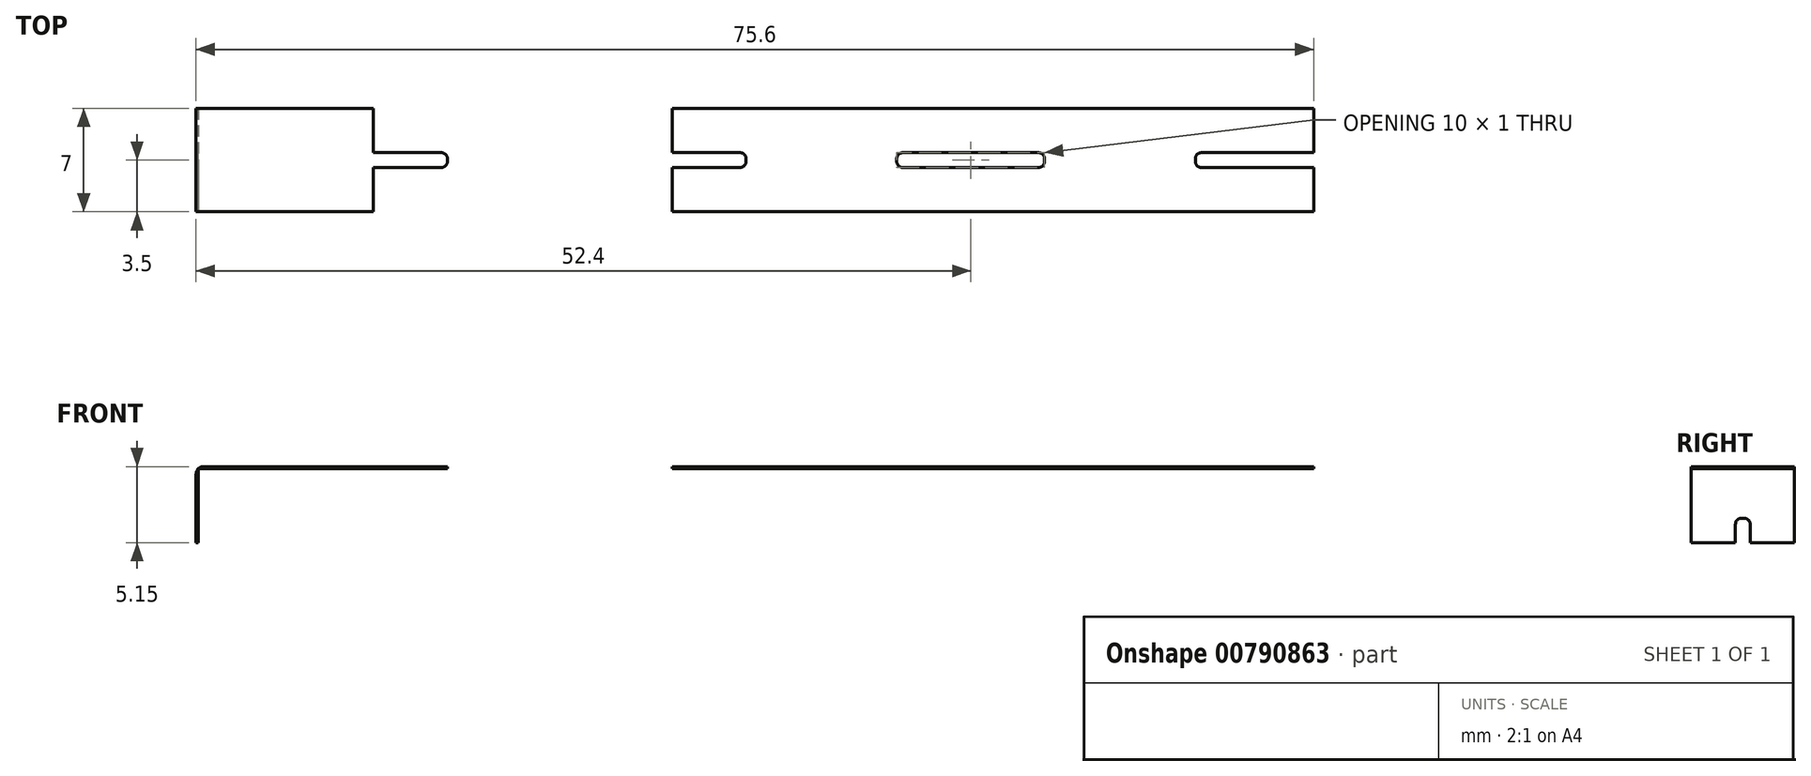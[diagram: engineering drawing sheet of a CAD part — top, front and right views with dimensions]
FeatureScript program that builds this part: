
annotation { "Feature Type Name" : "Feature", "Feature Type Description" : "" }
export const myFeature = defineFeature(function(context is Context, id is Id, definition is map)
    precondition{}
    {
        {
            var Q0;
            Q0=qCreatedBy(makeId("Top.planeOp"),FACE);
            var sketch = newSketch(context, id + "F0", { "sketchPlane" : qUnion([Q0])});
            skPoint(sketch, "E0.middle", {"position": v(0, 0) * mm});
            skLineSegment(sketch, "E1.bottom", {"start": v(-5.5, -0.5) * mm, "end": v(-10.1, -0.5) * mm});
            skLineSegment(sketch, "E1.top", {"start": v(-5.5, 0.5) * mm, "end": v(-10.1, 0.5) * mm});
            skLineSegment(sketch, "E1.left", {"start": v(-5.1, -0.1) * mm, "end": v(-5.1, 0.1) * mm});
            skLineSegment(sketch, "E1.right", {"start": v(-15.1, -0.1) * mm, "end": v(-15.1, 0.1) * mm});
            skPoint(sketch, "E1.middle", {"position": v(-10.1, 0) * mm});
            skPoint(sketch, "E2.visualSharp", {"position": v(-5.1, 0.5) * mm});
            skArc(sketch, "E2.filletArc", {"start": v(-5.1, 0.1) * mm, "mid": v(-5.22, 0.38) * mm, "end": v(-5.5, 0.5) * mm});
            skPoint(sketch, "E3.visualSharp", {"position": v(-5.1, -0.5) * mm});
            skArc(sketch, "E3.filletArc", {"start": v(-5.5, -0.5) * mm, "mid": v(-5.22, -0.38) * mm, "end": v(-5.1, -0.1) * mm});
            skPoint(sketch, "E4.visualSharp", {"position": v(-15.1, 0.5) * mm});
            skArc(sketch, "E4.filletArc", {"start": v(-14.7, 0.5) * mm, "mid": v(-14.98, 0.38) * mm, "end": v(-15.1, 0.1) * mm});
            skPoint(sketch, "E5.visualSharp", {"position": v(-15.1, -0.5) * mm});
            skArc(sketch, "E5.filletArc", {"start": v(-15.1, -0.1) * mm, "mid": v(-14.98, -0.38) * mm, "end": v(-14.7, -0.5) * mm});
            skLineSegment(sketch, "E6", {"start": v(0, 3.5) * mm, "end": v(-10.1, 3.5) * mm});
            skPoint(sketch, "E6.endSnap0", {"position": v(-10.1, 0.5) * mm});
            skLineSegment(sketch, "E7", {"start": v(-10.1, 3.5) * mm, "end": v(-10.1, 0.5) * mm});
            skLineSegment(sketch, "E8.MirrorCS", {"start": v(0, -3.5) * mm, "end": v(-10.1, -3.5) * mm});
            skLineSegment(sketch, "E9.MirrorCS", {"start": v(-10.1, -3.5) * mm, "end": v(-10.1, -0.5) * mm});
            skLineSegment(sketch, "E10.MirrorCS", {"start": v(0, 3.5) * mm, "end": v(10.1, 3.5) * mm});
            skLineSegment(sketch, "E11.MirrorCS", {"start": v(0, -3.5) * mm, "end": v(10.1, -3.5) * mm});
            skLineSegment(sketch, "E12.MirrorCS", {"start": v(5.1, -0.1) * mm, "end": v(5.1, 0.1) * mm});
            skArc(sketch, "E13.MirrorCS", {"start": v(5.1, 0.1) * mm, "mid": v(5.22, 0.38) * mm, "end": v(5.5, 0.5) * mm});
            skArc(sketch, "E14.MirrorCS", {"start": v(15.1, -0.1) * mm, "mid": v(14.98, -0.38) * mm, "end": v(14.7, -0.5) * mm});
            skLineSegment(sketch, "E15.MirrorCS", {"start": v(15.1, -0.1) * mm, "end": v(15.1, 0.1) * mm});
            skArc(sketch, "E16.MirrorCS", {"start": v(14.7, 0.5) * mm, "mid": v(14.98, 0.38) * mm, "end": v(15.1, 0.1) * mm});
            skArc(sketch, "E17.MirrorCS", {"start": v(5.5, -0.5) * mm, "mid": v(5.22, -0.38) * mm, "end": v(5.1, -0.1) * mm});
            skPoint(sketch, "E18.MirrorP", {"position": v(15.1, 0.5) * mm});
            skLineSegment(sketch, "E19.MirrorCS", {"start": v(5.5, 0.5) * mm, "end": v(14.7, 0.5) * mm});
            skLineSegment(sketch, "E20.MirrorCS", {"start": v(5.5, -0.5) * mm, "end": v(14.7, -0.5) * mm});
            skPoint(sketch, "E21.MirrorP", {"position": v(10.1, 0.5) * mm});
            skPoint(sketch, "E22.MirrorP", {"position": v(5.1, 0.5) * mm});
            skPoint(sketch, "E23.MirrorP", {"position": v(15.1, -0.5) * mm});
            skPoint(sketch, "E24.MirrorP", {"position": v(5.1, -0.5) * mm});
            skPoint(sketch, "E25.MirrorP", {"position": v(10.1, 0) * mm});
            skLineSegment(sketch, "E26.MirrorCS", {"start": v(10.1, 3.5) * mm, "end": v(10.1, 0.5) * mm});
            skLineSegment(sketch, "E27.MirrorCS", {"start": v(10.1, -3.5) * mm, "end": v(10.1, -0.5) * mm});
            skPoint(sketch, "E28.1.0.0", {"position": v(25.3, 0.5) * mm});
            skLineSegment(sketch, "E28.1.0.1", {"start": v(20.2, 3.5) * mm, "end": v(30.3, 3.5) * mm});
            skLineSegment(sketch, "E28.1.0.2", {"start": v(25.7, -0.5) * mm, "end": v(34.9, -0.5) * mm});
            skPoint(sketch, "E28.1.0.3", {"position": v(20.2, 0) * mm});
            skLineSegment(sketch, "E28.1.0.4", {"start": v(20.2, -3.5) * mm, "end": v(30.3, -3.5) * mm});
            skPoint(sketch, "E28.1.0.5", {"position": v(30.3, 0.5) * mm});
            skPoint(sketch, "E28.1.0.6", {"position": v(30.3, 0) * mm});
            skPoint(sketch, "E28.1.0.7", {"position": v(35.3, -0.5) * mm});
            skPoint(sketch, "E28.1.0.8", {"position": v(25.3, -0.5) * mm});
            skLineSegment(sketch, "E28.1.0.9", {"start": v(20.2, -3.5) * mm, "end": v(10.1, -3.5) * mm});
            skLineSegment(sketch, "E28.1.0.10", {"start": v(25.7, 0.5) * mm, "end": v(34.9, 0.5) * mm});
            skLineSegment(sketch, "E28.1.0.11", {"start": v(20.2, 3.5) * mm, "end": v(10.1, 3.5) * mm});
            skLineSegment(sketch, "E28.1.0.12", {"start": v(30.3, 3.5) * mm, "end": v(30.3, 0.5) * mm});
            skLineSegment(sketch, "E28.1.0.13", {"start": v(30.3, -3.5) * mm, "end": v(30.3, -0.5) * mm});
            skPoint(sketch, "E28.1.0.14", {"position": v(35.3, 0.5) * mm});
            skArc(sketch, "E28.1.0.15", {"start": v(34.9, 0.5) * mm, "mid": v(35.18, 0.38) * mm, "end": v(35.3, 0.1) * mm});
            skArc(sketch, "E28.1.0.16", {"start": v(25.7, -0.5) * mm, "mid": v(25.42, -0.38) * mm, "end": v(25.3, -0.1) * mm});
            skArc(sketch, "E28.1.0.17", {"start": v(35.3, -0.1) * mm, "mid": v(35.18, -0.38) * mm, "end": v(34.9, -0.5) * mm});
            skArc(sketch, "E28.1.0.18", {"start": v(25.3, 0.1) * mm, "mid": v(25.42, 0.38) * mm, "end": v(25.7, 0.5) * mm});
            skLineSegment(sketch, "E28.1.0.19", {"start": v(25.3, -0.1) * mm, "end": v(25.3, 0.1) * mm});
            skLineSegment(sketch, "E28.1.0.20", {"start": v(35.3, -0.1) * mm, "end": v(35.3, 0.1) * mm});
            skPoint(sketch, "E28.2.0.0", {"position": v(45.5, 0.5) * mm});
            skLineSegment(sketch, "E28.2.0.1", {"start": v(40.4, 3.5) * mm, "end": v(50.5, 3.5) * mm});
            skLineSegment(sketch, "E28.2.0.2", {"start": v(45.9, -0.5) * mm, "end": v(55.1, -0.5) * mm});
            skPoint(sketch, "E28.2.0.3", {"position": v(40.4, 0) * mm});
            skLineSegment(sketch, "E28.2.0.4", {"start": v(40.4, -3.5) * mm, "end": v(50.5, -3.5) * mm});
            skPoint(sketch, "E28.2.0.5", {"position": v(50.5, 0.5) * mm});
            skPoint(sketch, "E28.2.0.6", {"position": v(50.5, 0) * mm});
            skPoint(sketch, "E28.2.0.7", {"position": v(55.5, -0.5) * mm});
            skPoint(sketch, "E28.2.0.8", {"position": v(45.5, -0.5) * mm});
            skLineSegment(sketch, "E28.2.0.9", {"start": v(40.4, -3.5) * mm, "end": v(30.3, -3.5) * mm});
            skLineSegment(sketch, "E28.2.0.10", {"start": v(45.9, 0.5) * mm, "end": v(55.1, 0.5) * mm});
            skLineSegment(sketch, "E28.2.0.11", {"start": v(40.4, 3.5) * mm, "end": v(30.3, 3.5) * mm});
            skLineSegment(sketch, "E28.2.0.12", {"start": v(50.5, 3.5) * mm, "end": v(50.5, 0.5) * mm});
            skLineSegment(sketch, "E28.2.0.13", {"start": v(50.5, -3.5) * mm, "end": v(50.5, -0.5) * mm});
            skPoint(sketch, "E28.2.0.14", {"position": v(55.5, 0.5) * mm});
            skArc(sketch, "E28.2.0.15", {"start": v(55.1, 0.5) * mm, "mid": v(55.38, 0.38) * mm, "end": v(55.5, 0.1) * mm});
            skArc(sketch, "E28.2.0.16", {"start": v(45.9, -0.5) * mm, "mid": v(45.62, -0.38) * mm, "end": v(45.5, -0.1) * mm});
            skArc(sketch, "E28.2.0.17", {"start": v(55.5, -0.1) * mm, "mid": v(55.38, -0.38) * mm, "end": v(55.1, -0.5) * mm});
            skArc(sketch, "E28.2.0.18", {"start": v(45.5, 0.1) * mm, "mid": v(45.62, 0.38) * mm, "end": v(45.9, 0.5) * mm});
            skLineSegment(sketch, "E28.2.0.19", {"start": v(45.5, -0.1) * mm, "end": v(45.5, 0.1) * mm});
            skLineSegment(sketch, "E28.2.0.20", {"start": v(55.5, -0.1) * mm, "end": v(55.5, 0.1) * mm});
            skPoint(sketch, "E28.3.0.0", {"position": v(65.7, 0.5) * mm});
            skLineSegment(sketch, "E28.3.0.1", {"start": v(60.6, 3.5) * mm, "end": v(70.7, 3.5) * mm});
            skLineSegment(sketch, "E28.3.0.2", {"start": v(66.1, -0.5) * mm, "end": v(75.3, -0.5) * mm});
            skPoint(sketch, "E28.3.0.3", {"position": v(60.6, 0) * mm});
            skLineSegment(sketch, "E28.3.0.4", {"start": v(60.6, -3.5) * mm, "end": v(70.7, -3.5) * mm});
            skPoint(sketch, "E28.3.0.5", {"position": v(70.7, 0.5) * mm});
            skPoint(sketch, "E28.3.0.6", {"position": v(70.7, 0) * mm});
            skPoint(sketch, "E28.3.0.7", {"position": v(75.7, -0.5) * mm});
            skPoint(sketch, "E28.3.0.8", {"position": v(65.7, -0.5) * mm});
            skLineSegment(sketch, "E28.3.0.9", {"start": v(60.6, -3.5) * mm, "end": v(50.5, -3.5) * mm});
            skLineSegment(sketch, "E28.3.0.10", {"start": v(66.1, 0.5) * mm, "end": v(75.3, 0.5) * mm});
            skLineSegment(sketch, "E28.3.0.11", {"start": v(60.6, 3.5) * mm, "end": v(50.5, 3.5) * mm});
            skLineSegment(sketch, "E28.3.0.12", {"start": v(70.7, 3.5) * mm, "end": v(70.7, 0.5) * mm});
            skLineSegment(sketch, "E28.3.0.13", {"start": v(70.7, -3.5) * mm, "end": v(70.7, -0.5) * mm});
            skPoint(sketch, "E28.3.0.14", {"position": v(75.7, 0.5) * mm});
            skArc(sketch, "E28.3.0.15", {"start": v(75.3, 0.5) * mm, "mid": v(75.58, 0.38) * mm, "end": v(75.7, 0.1) * mm});
            skArc(sketch, "E28.3.0.16", {"start": v(66.1, -0.5) * mm, "mid": v(65.82, -0.38) * mm, "end": v(65.7, -0.1) * mm});
            skArc(sketch, "E28.3.0.17", {"start": v(75.7, -0.1) * mm, "mid": v(75.58, -0.38) * mm, "end": v(75.3, -0.5) * mm});
            skArc(sketch, "E28.3.0.18", {"start": v(65.7, 0.1) * mm, "mid": v(65.82, 0.38) * mm, "end": v(66.1, 0.5) * mm});
            skLineSegment(sketch, "E28.3.0.19", {"start": v(65.7, -0.1) * mm, "end": v(65.7, 0.1) * mm});
            skLineSegment(sketch, "E28.3.0.20", {"start": v(75.7, -0.1) * mm, "end": v(75.7, 0.1) * mm});
            skLineSegment(sketch, "E28.direction1", {"start": v(-10.1, -3.5) * mm, "end": v(10.1, -3.5) * mm, "construction": true});
            skLineSegment(sketch, "E29", {"start": v(0, 3.5) * mm, "end": v(0, -3.5) * mm});
            skLineSegment(sketch, "E30.bottom", {"start": v(70.7, -3.5) * mm, "end": v(73.7, -3.5) * mm});
            skLineSegment(sketch, "E30.top", {"start": v(70.7, 3.5) * mm, "end": v(73.7, 3.5) * mm});
            skLineSegment(sketch, "E30.left", {"start": v(70.7, -3.5) * mm, "end": v(70.7, 3.5) * mm});
            skLineSegment(sketch, "E30.right", {"start": v(73.7, -3.5) * mm, "end": v(73.7, 3.5) * mm});
            skSolve(sketch);
        }
        {
            var Q0;
            {var subQ8=sQuery(id+"F0.wireOp",EDGE,"E28.3.0.12");Q0=makeQuery(id+"F0.imprint","IMPRINT",FACE,{"disambiguationData":[TD([[makeQuery(id+"F0.imprint","IMPRINT",EDGE,{"derivedFrom":subQ8}),1.0]])]});}
            var Q1;
            {var subQ3=sQuery(id+"F0.wireOp",EDGE,"E14.MirrorCS");Q1=makeQuery(id+"F0.imprint","IMPRINT",FACE,{"disambiguationData":[TD([[makeQuery(id+"F0.imprint","IMPRINT",EDGE,{"derivedFrom":subQ3}),1.0]])]});}
            var Q2;
            {var subQ8=sQuery(id+"F0.wireOp",EDGE,"E28.1.0.12");Q2=makeQuery(id+"F0.imprint","IMPRINT",FACE,{"disambiguationData":[TD([[makeQuery(id+"F0.imprint","IMPRINT",EDGE,{"derivedFrom":subQ8}),1.0]])]});}
            var Q3;
            {var subQ8=sQuery(id+"F0.wireOp",EDGE,"E28.2.0.12");Q3=makeQuery(id+"F0.imprint","IMPRINT",FACE,{"disambiguationData":[TD([[makeQuery(id+"F0.imprint","IMPRINT",EDGE,{"derivedFrom":subQ8}),1.0]])]});}
            var Q4;
            Q4=makeQuery(id+"F0.imprint","IMPRINT",FACE,{"disambiguationData":[TD([[makeQuery(id+"F0.imprint","IMPRINT",EDGE,{"derivedFrom":sQuery(id+"F0.wireOp",EDGE,"E10.MirrorCS")}),-1.0]])]});
            var Q5;
            {var subQ5=sQuery(id+"F0.wireOp",EDGE,"E30.top");Q5=makeQuery(id+"F0.imprint","IMPRINT",FACE,{"disambiguationData":[TD([[makeQuery(id+"F0.imprint","IMPRINT",EDGE,{"derivedFrom":subQ5}),-1.0]])]});}
            var Q6;
            {var subQ5=sQuery(id+"F0.wireOp",EDGE,"E30.bottom");Q6=makeQuery(id+"F0.imprint","IMPRINT",FACE,{"disambiguationData":[TD([[makeQuery(id+"F0.imprint","IMPRINT",EDGE,{"derivedFrom":subQ5}),1.0]])]});}
            extrude(context, id + "F1", {"entities" : qUnion([Q0, Q1, Q2, Q3, Q4, Q5, Q6]), "depth" : 0.15 * mm, "offsetDistance" : 25 * mm});
        }
        {
            var Q0;
            Q0=makeQuery(id+"F1.opExtrude","SWEPT_FACE",FACE,{"disambiguationData":[OSD([sQuery(id+"F0.wireOp",EDGE,"E29")])]});
            extrude(context, id + "F2", {"entities" : qUnion([Q0]), "operationType" : NewBodyOperationType.ADD, "depth" : 1.9 * mm, "offsetDistance" : 25 * mm});
        }
        {
            var Q0;
            {var subQ0=sQuery(id+"F0.wireOp",EDGE,"E29");Q0=makeQuery(id+"F2.boolean.opBoolean","MERGE",FACE,{"derivedFrom":[makeQuery(id+"F1.opExtrude","CAP_FACE",FACE,{"disambiguationData":[OSD([sQuery(id+"F0.wireOp",EDGE,"E10.MirrorCS"),sQuery(id+"F0.wireOp",EDGE,"E11.MirrorCS"),sQuery(id+"F0.wireOp",EDGE,"E12.MirrorCS"),sQuery(id+"F0.wireOp",EDGE,"E13.MirrorCS"),sQuery(id+"F0.wireOp",EDGE,"E14.MirrorCS"),sQuery(id+"F0.wireOp",EDGE,"E15.MirrorCS"),sQuery(id+"F0.wireOp",EDGE,"E16.MirrorCS"),sQuery(id+"F0.wireOp",EDGE,"E17.MirrorCS"),sQuery(id+"F0.wireOp",EDGE,"E19.MirrorCS"),sQuery(id+"F0.wireOp",EDGE,"E20.MirrorCS"),sQuery(id+"F0.wireOp",EDGE,"E28.1.0.1"),sQuery(id+"F0.wireOp",EDGE,"E28.1.0.2"),sQuery(id+"F0.wireOp",EDGE,"E28.1.0.4"),sQuery(id+"F0.wireOp",EDGE,"E28.1.0.9"),sQuery(id+"F0.wireOp",EDGE,"E28.1.0.10"),sQuery(id+"F0.wireOp",EDGE,"E28.1.0.11"),sQuery(id+"F0.wireOp",EDGE,"E28.1.0.15"),sQuery(id+"F0.wireOp",EDGE,"E28.1.0.16"),sQuery(id+"F0.wireOp",EDGE,"E28.1.0.17"),sQuery(id+"F0.wireOp",EDGE,"E28.1.0.18"),sQuery(id+"F0.wireOp",EDGE,"E28.1.0.19"),sQuery(id+"F0.wireOp",EDGE,"E28.1.0.20"),sQuery(id+"F0.wireOp",EDGE,"E28.2.0.1"),sQuery(id+"F0.wireOp",EDGE,"E28.2.0.2"),sQuery(id+"F0.wireOp",EDGE,"E28.2.0.4"),sQuery(id+"F0.wireOp",EDGE,"E28.2.0.9"),sQuery(id+"F0.wireOp",EDGE,"E28.2.0.10"),sQuery(id+"F0.wireOp",EDGE,"E28.2.0.11"),sQuery(id+"F0.wireOp",EDGE,"E28.2.0.15"),sQuery(id+"F0.wireOp",EDGE,"E28.2.0.16"),sQuery(id+"F0.wireOp",EDGE,"E28.2.0.17"),sQuery(id+"F0.wireOp",EDGE,"E28.2.0.18"),sQuery(id+"F0.wireOp",EDGE,"E28.2.0.19"),sQuery(id+"F0.wireOp",EDGE,"E28.2.0.20"),sQuery(id+"F0.wireOp",EDGE,"E28.3.0.1"),sQuery(id+"F0.wireOp",EDGE,"E28.3.0.2"),sQuery(id+"F0.wireOp",EDGE,"E28.3.0.4"),sQuery(id+"F0.wireOp",EDGE,"E28.3.0.9"),sQuery(id+"F0.wireOp",EDGE,"E28.3.0.10"),sQuery(id+"F0.wireOp",EDGE,"E28.3.0.11"),sQuery(id+"F0.wireOp",EDGE,"E28.3.0.12"),sQuery(id+"F0.wireOp",EDGE,"E28.3.0.13"),sQuery(id+"F0.wireOp",EDGE,"E28.3.0.16"),sQuery(id+"F0.wireOp",EDGE,"E28.3.0.18"),sQuery(id+"F0.wireOp",EDGE,"E28.3.0.19"),subQ0])],"isStart":true}),makeQuery(id+"F2.opExtrude","SWEPT_FACE",FACE,{"disambiguationData":[OSD([subQ0]),TDD([makeQuery(id+"F1.opExtrude","CAP_EDGE",EDGE,{"disambiguationData":[OSD([subQ0])],"isStart":true})])]})]});}
            var sketch = newSketch(context, id + "F3", { "sketchPlane" : qUnion([Q0])});
            skLineSegment(sketch, "E31.bottom", {"start": v(-1.9, -3.5) * mm, "end": v(-1.75, -3.5) * mm});
            skLineSegment(sketch, "E31.top", {"start": v(-1.9, 3.5) * mm, "end": v(-1.75, 3.5) * mm});
            skLineSegment(sketch, "E31.left", {"start": v(-1.9, -3.5) * mm, "end": v(-1.9, 3.5) * mm});
            skLineSegment(sketch, "E31.right", {"start": v(-1.75, -3.5) * mm, "end": v(-1.75, 3.5) * mm});
            skSolve(sketch);
        }
        {
            var Q0;
            Q0 = qSketchRegion(id + "F3", true);
            extrude(context, id + "F4", {"entities" : qUnion([Q0]), "operationType" : NewBodyOperationType.ADD, "depth" : 5 * mm, "offsetDistance" : 25 * mm});
        }
        {
            var Q0;
            Q0=makeQuery(id+"F4.boolean.opBoolean","MERGE",FACE,{"derivedFrom":[makeQuery(id+"F2.opExtrude","CAP_FACE",FACE,{"disambiguationData":[OSD([sQuery(id+"F0.wireOp",EDGE,"E29")])],"isStart":false}),makeQuery(id+"F4.opExtrude","SWEPT_FACE",FACE,{"disambiguationData":[OSD([sQuery(id+"F3.wireOp",EDGE,"E31.left")])]})]});
            var sketch = newSketch(context, id + "F5", { "sketchPlane" : qUnion([Q0])});
            skLineSegment(sketch, "E32.bottom", {"start": v(0.1, -3.35) * mm, "end": v(-0.1, -3.35) * mm});
            skLineSegment(sketch, "E32.top", {"start": v(0.5, -13.35) * mm, "end": v(-0.5, -13.35) * mm});
            skLineSegment(sketch, "E32.left", {"start": v(0.5, -3.75) * mm, "end": v(0.5, -13.35) * mm});
            skLineSegment(sketch, "E32.right", {"start": v(-0.5, -3.75) * mm, "end": v(-0.5, -13.35) * mm});
            skPoint(sketch, "E32.middle", {"position": v(0, -8.35) * mm});
            skPoint(sketch, "E32.middle.positionSnap0", {"position": v(0, -5) * mm});
            skPoint(sketch, "E32.centerSnap0", {"position": v(0, -5) * mm});
            skPoint(sketch, "E33.visualSharp", {"position": v(-0.5, -3.35) * mm});
            skArc(sketch, "E33.filletArc", {"start": v(-0.1, -3.35) * mm, "mid": v(-0.38, -3.47) * mm, "end": v(-0.5, -3.75) * mm});
            skPoint(sketch, "E34.visualSharp", {"position": v(0.5, -3.35) * mm});
            skArc(sketch, "E34.filletArc", {"start": v(0.5, -3.75) * mm, "mid": v(0.38, -3.47) * mm, "end": v(0.1, -3.35) * mm});
            skSolve(sketch);
        }
        {
            var Q0;
            Q0=makeQuery(id+"F5.imprint","IMPRINT",FACE,{"disambiguationData":[TD([[makeQuery(id+"F5.imprint","IMPRINT",EDGE,{"derivedFrom":sQuery(id+"F5.wireOp",EDGE,"E32.bottom")}),1.0]])]});
            extrude(context, id + "F6", {"entities" : qUnion([Q0]), "operationType" : NewBodyOperationType.REMOVE, "oppositeDirection" : true, "depth" : 25 * mm, "offsetDistance" : 25 * mm});
        }
        {
            var Q0;
            {var subQ0=sQuery(id+"F0.wireOp",EDGE,"E29");Q0=makeQuery(id+"F2.opExtrude","CAP_EDGE",EDGE,{"disambiguationData":[OSD([subQ0]),TDD([makeQuery(id+"F1.opExtrude","CAP_EDGE",EDGE,{"disambiguationData":[OSD([subQ0])],"isStart":false})])],"isStart":false});}
            var Q1;
            Q1=makeQuery(id+"F4.opExtrude","CAP_EDGE",EDGE,{"disambiguationData":[OSD([sQuery(id+"F3.wireOp",EDGE,"E31.right")])],"isStart":true});
            fillet(context, id + "F7", {"entities" : qUnion([Q0, Q1]), "radius" : 0.5 * mm, "tangentPropagation" : true, "allowEdgeOverflow" : false});
        }
    });
